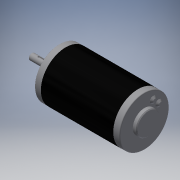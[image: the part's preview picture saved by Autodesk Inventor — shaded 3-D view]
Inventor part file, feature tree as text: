
AUTODESK INVENTOR PART (.ipt)
format: ipt  version: 2017 (Build 210142000, 142)  size: 167,424 bytes
history: native  units: in
note: dims shown in document units (in); Inventor stores cm internally (conversion verified against a paired STEP export)
features: chamfer x1
ambient origin geometry x8: Origin, YZ Plane, XZ Plane, XY Plane, X Axis, Y Axis, Z Axis, Center Point
bodies: Solid1 (feature_tree)
feature tree (1):
  chamfer  "Chamfer3"  [1 undecoded]
note: 1 required parameter value undecoded (feature->parameter linkage not recoverable at this tier; creation-order binding heuristic only, values carry confidence <= 0.55)
